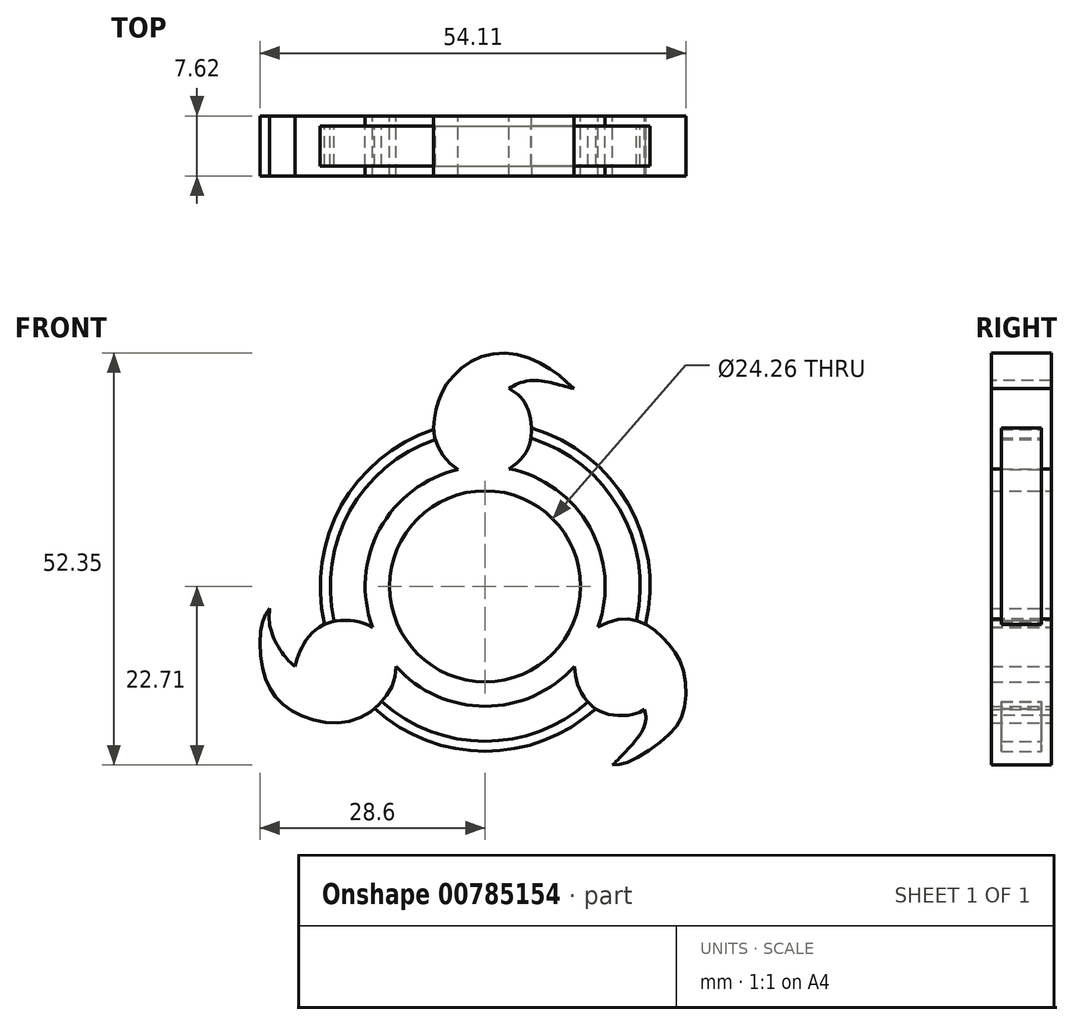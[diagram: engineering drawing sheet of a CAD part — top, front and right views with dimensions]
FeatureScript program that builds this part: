
annotation { "Feature Type Name" : "Feature", "Feature Type Description" : "" }
export const myFeature = defineFeature(function(context is Context, id is Id, definition is map)
    precondition{}
    {
        {
            var Q0;
            Q0=qCreatedBy(makeId("Front.planeOp"),FACE);
            var sketch = newSketch(context, id + "F0", { "sketchPlane" : qUnion([Q0])});
            skCircle(sketch, "E0", {"center": v(0, 0) * mm, "radius": 15.24 * mm});
            skCircle(sketch, "E1", {"center": v(0, 0) * mm, "radius": 12.13 * mm});
            skSolve(sketch);
        }
        {
            var Q0;
            Q0=qCreatedBy(makeId("Front.planeOp"),FACE);
            var sketch = newSketch(context, id + "F1", { "sketchPlane" : qUnion([Q0])});
            skCircle(sketch, "E2", {"center": v(0, 0) * mm, "radius": 20.96 * mm});
            skCircle(sketch, "E3", {"center": v(0, 0) * mm, "radius": 19.69 * mm});
            skSolve(sketch);
        }
        {
            var Q0;
            Q0=qSketchRegion(id+"F1",true);
            extrude(context, id + "F2", {"entities" : qUnion([Q0]), "depth" : 3.8 * mm, "offsetDistance" : 25.4 * mm});
        }
        {
            var Q0;
            Q0=qSketchRegion(id+"F0",true);
            extrude(context, id + "F3", {"entities" : qUnion([Q0]), "operationType" : NewBodyOperationType.ADD, "depth" : 5.08 * mm});
        }
        {
            var Q0;
            Q0=qCreatedBy(makeId("Front.planeOp"),FACE);
            var sketch = newSketch(context, id + "F4", { "sketchPlane" : qUnion([Q0])});
            skFitSpline(sketch, "E4", {"points": [v(20.26, -15.67) * mm, v(19, -16.23) * mm, v(15.99, -16.33) * mm, v(13.64, -15.25) * mm, v(11.95, -13.04) * mm, v(11.34, -10.23) * mm, v(11.81, -7.79) * mm, v(14.53, -5.07) * mm, v(18.15, -4.18) * mm, v(21.29, -5.4) * mm, v(23.73, -7.88) * mm, v(25.28, -10.98) * mm, v(25.14, -16.05) * mm, v(22.98, -19.14) * mm, v(18.29, -22.29) * mm, v(16.18, -22.7) * mm], "startDerivative": vector(-24.78, -14.45) * mm, "endDerivative": vector(-34.66, -2.02) * mm});
            skFitSpline(sketch, "E5", {"points": [v(20.26, -15.67) * mm, v(20.26, -17.69) * mm, v(17.96, -20.88) * mm, v(16.18, -22.7) * mm], "startDerivative": vector(1.33, -6.74) * mm, "endDerivative": vector(-5.12, -5.1) * mm});
            skFitSpline(sketch, "E6", {"points": [v(3.05, 25.14) * mm, v(4.88, 23.55) * mm, v(5.86, 20.36) * mm, v(5.11, 16.93) * mm, v(1.92, 14.35) * mm, v(-1.5, 14.07) * mm, v(-4.74, 15.85) * mm, v(-6.48, 19.28) * mm, v(-6.24, 22.42) * mm, v(-5.11, 25.33) * mm, v(-1.92, 28.47) * mm, v(3.05, 29.6) * mm, v(8.16, 27.68) * mm, v(11.26, 25.1) * mm], "startDerivative": vector(32.58, -21.63) * mm, "endDerivative": vector(35.17, -33.59) * mm});
            skFitSpline(sketch, "E7", {"points": [v(11.26, 25.1) * mm, v(9.15, 25.66) * mm, v(6.8, 26.13) * mm, v(4.55, 25.9) * mm, v(3.05, 25.14) * mm], "startDerivative": vector(-8.21, 2.2) * mm, "endDerivative": vector(-6.28, -3.82) * mm});
            skFitSpline(sketch, "E8", {"points": [v(-23.92, -10.35) * mm, v(-24.72, -9.71) * mm, v(-26.06, -8.06) * mm, v(-27.34, -5.12) * mm, v(-27.4, -2.83) * mm], "startDerivative": vector(-4.4, 3.18) * mm, "endDerivative": vector(0.68, 8.42) * mm});
            skFitSpline(sketch, "E9", {"points": [v(-27.4, -2.83) * mm, v(-28.4, -5.02) * mm, v(-28.2, -10.73) * mm, v(-26.16, -14.57) * mm, v(-21.62, -17.03) * mm, v(-16.07, -16.76) * mm, v(-12.23, -13.4) * mm, v(-11.42, -9.4) * mm, v(-13.77, -5.6) * mm, v(-17.35, -4.32) * mm, v(-20.88, -5.07) * mm, v(-23.17, -7.52) * mm, v(-24.18, -10.17) * mm], "startDerivative": vector(-18.88, -28.65) * mm, "endDerivative": vector(-11.45, -38.62) * mm});
            skSolve(sketch);
        }
        {
            var Q0;
            Q0=qSketchRegion(id+"F4",true);
            extrude(context, id + "F5", {"entities" : qUnion([Q0]), "operationType" : NewBodyOperationType.ADD, "depth" : 5.08 * mm, "offsetDistance" : 25.4 * mm});
        }
        {
            var Q0;
            Q0=makeQuery(id+"F5.opExtrude","CAP_FACE",FACE,{"disambiguationData":[OSD([sQuery(id+"F4.wireOp",EDGE,"E6"),sQuery(id+"F4.wireOp",EDGE,"E7")])],"isStart":false});
            var Q1;
            Q1=makeQuery(id+"F5.opExtrude","CAP_FACE",FACE,{"disambiguationData":[OSD([sQuery(id+"F4.wireOp",EDGE,"E8"),sQuery(id+"F4.wireOp",EDGE,"E9")])],"isStart":false});
            var Q2;
            Q2=makeQuery(id+"F5.opExtrude","CAP_FACE",FACE,{"disambiguationData":[OSD([sQuery(id+"F4.wireOp",EDGE,"E4"),sQuery(id+"F4.wireOp",EDGE,"E5")])],"isStart":false});
            var Q3;
            Q3=makeQuery(id+"F3.opExtrude","CAP_FACE",FACE,{"disambiguationData":[OSD([sQuery(id+"F0.wireOp",EDGE,"E0")])],"isStart":false});
            extrude(context, id + "F6", {"entities" : qUnion([Q0, Q1, Q2, Q3]), "operationType" : NewBodyOperationType.ADD, "oppositeDirection" : true, "depth" : 7.62 * mm, "offsetDistance" : 25.4 * mm});
        }
        {
            var Q0;
            {var subQ0=sQuery(id+"F1.wireOp",EDGE,"E2");var subQ1=sQuery(id+"F1.wireOp",EDGE,"E3");Q0=makeQuery(id+"F5.boolean.opBoolean","SPLIT",FACE,{"disambiguationData":[TD([makeQuery(id+"F2.opExtrude","SWEPT_FACE",FACE,{"disambiguationData":[OSD([subQ0])]}),makeQuery(id+"F2.opExtrude","SWEPT_FACE",FACE,{"disambiguationData":[OSD([subQ1])]}),makeQuery(id+"F5.opExtrude","SWEPT_FACE",FACE,{"disambiguationData":[OSD([sQuery(id+"F4.wireOp",EDGE,"E4")])]}),makeQuery(id+"F5.opExtrude","SWEPT_FACE",FACE,{"disambiguationData":[OSD([sQuery(id+"F4.wireOp",EDGE,"E9")])]})])],"derivedFrom":makeQuery(id+"F2.opExtrude","CAP_FACE",FACE,{"disambiguationData":[OSD([subQ0,subQ1])],"isStart":false})});}
            var Q1;
            {var subQ0=sQuery(id+"F1.wireOp",EDGE,"E2");var subQ1=sQuery(id+"F1.wireOp",EDGE,"E3");Q1=makeQuery(id+"F5.boolean.opBoolean","SPLIT",FACE,{"disambiguationData":[TD([makeQuery(id+"F2.opExtrude","SWEPT_FACE",FACE,{"disambiguationData":[OSD([subQ0])]}),makeQuery(id+"F2.opExtrude","SWEPT_FACE",FACE,{"disambiguationData":[OSD([subQ1])]}),makeQuery(id+"F5.opExtrude","SWEPT_FACE",FACE,{"disambiguationData":[OSD([sQuery(id+"F4.wireOp",EDGE,"E4")])]}),makeQuery(id+"F5.opExtrude","SWEPT_FACE",FACE,{"disambiguationData":[OSD([sQuery(id+"F4.wireOp",EDGE,"E6")])]})])],"derivedFrom":makeQuery(id+"F2.opExtrude","CAP_FACE",FACE,{"disambiguationData":[OSD([subQ0,subQ1])],"isStart":false})});}
            var Q2;
            {var subQ0=sQuery(id+"F1.wireOp",EDGE,"E2");var subQ1=sQuery(id+"F1.wireOp",EDGE,"E3");Q2=makeQuery(id+"F5.boolean.opBoolean","SPLIT",FACE,{"disambiguationData":[TD([makeQuery(id+"F2.opExtrude","SWEPT_FACE",FACE,{"disambiguationData":[OSD([subQ0])]}),makeQuery(id+"F2.opExtrude","SWEPT_FACE",FACE,{"disambiguationData":[OSD([subQ1])]}),makeQuery(id+"F5.opExtrude","SWEPT_FACE",FACE,{"disambiguationData":[OSD([sQuery(id+"F4.wireOp",EDGE,"E6")])]}),makeQuery(id+"F5.opExtrude","SWEPT_FACE",FACE,{"disambiguationData":[OSD([sQuery(id+"F4.wireOp",EDGE,"E9")])]})])],"derivedFrom":makeQuery(id+"F2.opExtrude","CAP_FACE",FACE,{"disambiguationData":[OSD([subQ0,subQ1])],"isStart":false})});}
            extrude(context, id + "F7", {"entities" : qUnion([Q0, Q1, Q2]), "operationType" : NewBodyOperationType.ADD, "oppositeDirection" : true, "depth" : 5.08 * mm, "offsetDistance" : 25.4 * mm});
        }
    });
